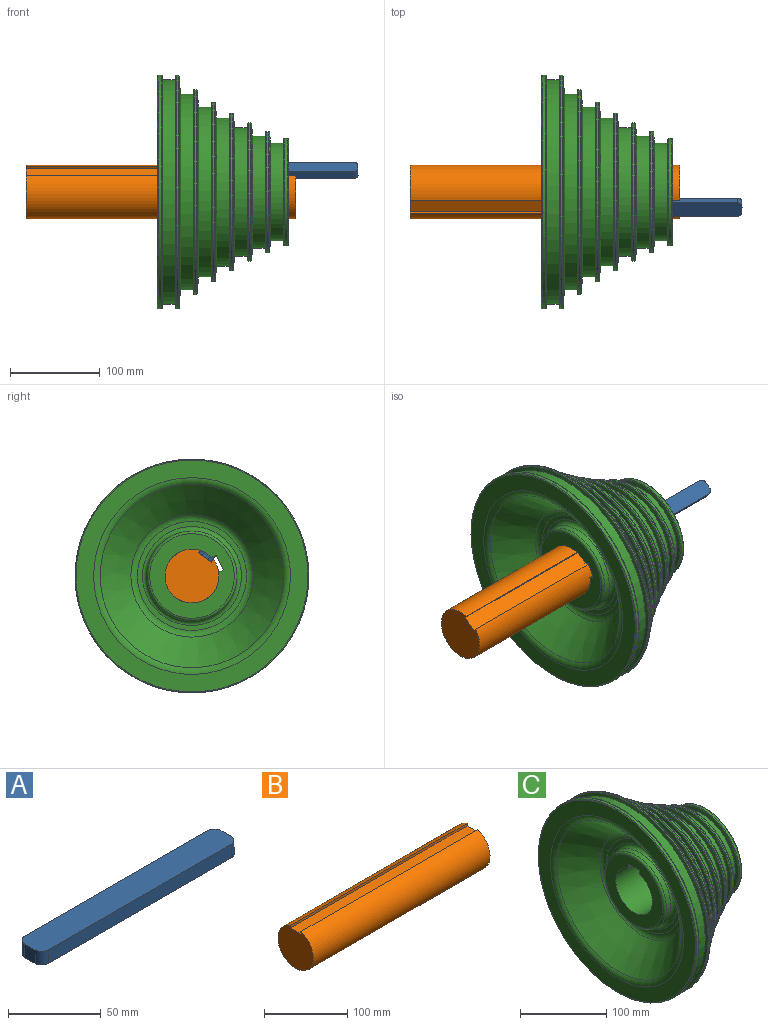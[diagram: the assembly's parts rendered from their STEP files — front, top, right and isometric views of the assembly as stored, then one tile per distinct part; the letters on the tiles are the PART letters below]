
ASSEMBLY  parts=3 mates=3
PART A: 10 faces, bbox 150x17.9x9 mm
  f0: plane 150x17.9mm, normal (0,0,-1), area 2663.5mm2, adj f1,f3,f4,f5,f6,f7,f8,f9
  f1: plane 140x9mm, normal (0,1,0), area 1260mm2, adj f0,f2,f6,f8
  f2: plane 150x17.9mm, normal (0,0,1), area 2663.5mm2, adj f1,f3,f4,f5,f6,f7,f8,f9
  f3: plane 140x9mm, normal (0,-1,0), area 1260mm2, adj f0,f2,f7,f9
  f4: plane 9x7.9mm, normal (1,0,0), area 71.1mm2, adj f0,f2,f8,f9
  f5: plane 9x7.9mm, normal (-1,0,0), area 71.1mm2, adj f0,f2,f6,f7
  f6: cylinder r=5mm len=9mm, axis (0,0,1), area 70.7mm2, adj f0,f1,f2,f5
  f7: cylinder r=5mm len=9mm, axis (0,0,-1), area 70.7mm2, adj f0,f2,f3,f5
  f8: cylinder r=5mm len=9mm, axis (0,0,-1), area 70.7mm2, adj f0,f1,f2,f4
  f9: cylinder r=5mm len=9mm, axis (0,0,1), area 70.7mm2, adj f0,f2,f3,f4
PART B: 6 faces, bbox 300x60x58.6 mm
  f0: plane 300x18mm, normal (0,0,1), area 5400mm2, adj f1,f3,f4,f5
  f1: plane 300x3.62mm, normal (0,1,0), area 1085.5mm2, adj f0,f2,f4,f5
  f2: cylinder r=30mm len=300mm, axis (-1,0,0), area 51064.2mm2, adj f1,f3,f4,f5
  f3: plane 300x3.62mm, normal (0,-1,0), area 1085.5mm2, adj f0,f2,f4,f5
  f4: plane 60x58.62mm, normal (1,0,0), area 2745.6mm2, adj f0,f1,f2,f3
  f5: plane 60x58.62mm, normal (-1,0,0), area 2745.6mm2, adj f0,f1,f2,f3
PART C: 60 faces, bbox 146x281.4x281.4 mm
  f0: cylinder r=30mm len=114mm, axis (-1,0,0), area 19404.4mm2, adj f1,f3,f35,f39
  f1: plane 118x5.78mm, normal (0,-1,0), area 673.9mm2, adj f0,f2,f4,f35,f39
  f2: plane 118x18mm, normal (0,0,-1), area 2124mm2, adj f1,f3,f4,f35
  f3: plane 118x5.78mm, normal (0,1,0), area 673.9mm2, adj f0,f2,f4,f35,f39
  f4: plane 117.1x117.1mm, normal (1,0,0), area 7123.6mm2, adj f1,f2,f3,f39,f58
  f5: plane 258x258mm, normal (-1,0,0), area 14710.2mm2, adj f40,f59
  f6: cylinder r=67.35mm len=134.7mm, axis (-1,0,0), area 932.6mm2, adj f47,f52
  f7: cylinder r=87.55mm len=175.1mm, axis (-1,0,0), area 1062.7mm2, adj f49,f54
  f8: cone r=82.3mm half-angle=85deg, axis (-1,0,0), area 9477.7mm2, adj f9,f55
  f9: cylinder r=82.3mm len=164.6mm, axis (1,0,0), area 7235.2mm2, adj f8,f10
  f10: cone r=82.3mm half-angle=80deg, axis (1,0,0), area 2385.2mm2, adj f9,f54
  f11: cylinder r=99.8mm len=199.6mm, axis (-1,0,0), area 1379mm2, adj f50,f55
  f12: cone r=94.46mm half-angle=85.2deg, axis (-1,0,0), area 12186.3mm2, adj f13,f51
  f13: cone r=94.46mm half-angle=0.2deg, axis (-1,0,0), area 8307.2mm2, adj f12,f14
  f14: cone r=94.42mm half-angle=85.4deg, axis (1,0,0), area 2719.3mm2, adj f13,f50
  f15: cylinder r=130mm len=260mm, axis (-1,0,0), area 1255.6mm2, adj f44,f57
  f16: cone r=108.75mm half-angle=85deg, axis (-1,0,0), area 15253.7mm2, adj f17,f57
  f17: cylinder r=108.75mm len=217.5mm, axis (1,0,0), area 9565.6mm2, adj f16,f18
  f18: cone r=108.75mm half-angle=83.4deg, axis (1,0,0), area 3062.8mm2, adj f17,f56
  f19: cylinder r=114mm len=228mm, axis (-1,0,0), area 1386mm2, adj f51,f56
  f20: cone r=71.6mm half-angle=85deg, axis (-1,0,0), area 7503.8mm2, adj f21,f49
  f21: cylinder r=71.6mm len=143.2mm, axis (1,0,0), area 6298.3mm2, adj f20,f22
  f22: cone r=71.6mm half-angle=80deg, axis (1,0,0), area 2083.2mm2, adj f21,f48
  f23: cone r=62.3mm half-angle=80deg, axis (1,0,0), area 1735.7mm2, adj f24,f52
  f24: cylinder r=62.3mm len=124.6mm, axis (1,0,0), area 5480.1mm2, adj f23,f25
  f25: cone r=62.3mm half-angle=85deg, axis (-1,0,0), area 5945mm2, adj f24,f53
  f26: cylinder r=76.85mm len=153.7mm, axis (-1,0,0), area 987.9mm2, adj f48,f53
  f27: cone r=54.2mm half-angle=85deg, axis (-1,0,0), area 4655.5mm2, adj f28,f47
  f28: cylinder r=54.2mm len=108.4mm, axis (1,0,0), area 4767.2mm2, adj f27,f29
  f29: cone r=54.2mm half-angle=80deg, axis (1,0,0), area 1629.6mm2, adj f28,f46
  f30: cylinder r=59.55mm len=119.1mm, axis (-1,0,0), area 1204.4mm2, adj f46,f58
  f31: cone r=125mm half-angle=80deg, axis (1,0,0), area 3384.1mm2, adj f33,f44
  f32: cone r=125mm half-angle=85deg, axis (-1,0,0), area 3275mm2, adj f33,f45
  f33: cylinder r=125mm len=250mm, axis (1,0,0), area 10995.6mm2, adj f31,f32
  f34: cylinder r=130mm len=260mm, axis (-1,0,0), area 2951mm2, adj f45,f59
  f35: plane 94x94mm, normal (-1,0,0), area 4024.9mm2, adj f0,f1,f2,f3,f43
  f36: cylinder r=50mm len=100mm, axis (-1,0,0), area 2199.1mm2, adj f42,f43
  f37: plane 121.29x121.29mm, normal (-1,0,0), area 2050.7mm2, adj f41,f42
  f38: cone r=105mm half-angle=42.9deg, axis (-1,0,0), area 26712.8mm2, adj f40,f41
  f39: cone r=30mm half-angle=45deg, axis (1,0,0), area 1034.2mm2, adj f0,f1,f3,f4
  f40: torus R=109.36mm, axis (-1,0,0), area 5444.3mm2, adj f5,f38
  f41: torus R=60.64mm, axis (-1,0,0), area 3330.7mm2, adj f37,f38
  f42: torus R=55mm, axis (-1,0,0), area 2557.1mm2, adj f36,f37
  f43: torus R=47mm, axis (-1,0,0), area 1448.2mm2, adj f35,f36
  f44: torus R=129mm, axis (1,0,0), area 1137.9mm2, adj f15,f31
  f45: torus R=129mm, axis (1,0,0), area 1208.7mm2, adj f32,f34
  f46: torus R=58.55mm, axis (1,0,0), area 519.8mm2, adj f29,f30
  f47: torus R=66.35mm, axis (1,0,0), area 624.7mm2, adj f6,f27
  f48: torus R=75.85mm, axis (1,0,0), area 671.6mm2, adj f22,f26
  f49: torus R=86.55mm, axis (1,0,0), area 813mm2, adj f7,f20
  f50: torus R=98.8mm, axis (1,0,0), area 931.9mm2, adj f11,f14
  f51: torus R=113mm, axis (1,0,0), area 1061.8mm2, adj f12,f19
  f52: torus R=66.35mm, axis (1,0,0), area 588.3mm2, adj f6,f23
  f53: torus R=75.85mm, axis (1,0,0), area 713.3mm2, adj f25,f26
  f54: torus R=86.55mm, axis (1,0,0), area 765.5mm2, adj f7,f10
  f55: torus R=98.8mm, axis (1,0,0), area 927.2mm2, adj f8,f11
  f56: torus R=113mm, axis (1,0,0), area 1039.6mm2, adj f18,f19
  f57: torus R=129mm, axis (1,0,0), area 1208.7mm2, adj f15,f16
  f58: torus R=58.55mm, axis (-1,0,0), area 584.1mm2, adj f4,f30
  f59: torus R=129mm, axis (-1,0,0), area 1279.5mm2, adj f5,f34
PLACE A rot(axis=(1,0,0),35deg) t=(-211.24,-222.14,-2.93)mm
PLACE B rot(axis=(1,0,0),35deg) t=(-430.43,-207.76,-23.38)mm
PLACE C rot(axis=(1,0,0),64.3deg) t=(-284.49,-207.76,-23.38)mm
MATE planar A.f3 <-> B.f1  axis (0,-0.82,-0.57) through (-136.24,-232.05,-4.37)mm
MATE planar B.f0 <-> A.f9  axis (0,-0.57,0.82) through (-280.43,-222.1,-2.9)mm
MATE cylindrical B.f2 <-> C.f0  axis (-1,0,0) through (-280.43,-207.76,-23.38)mm
